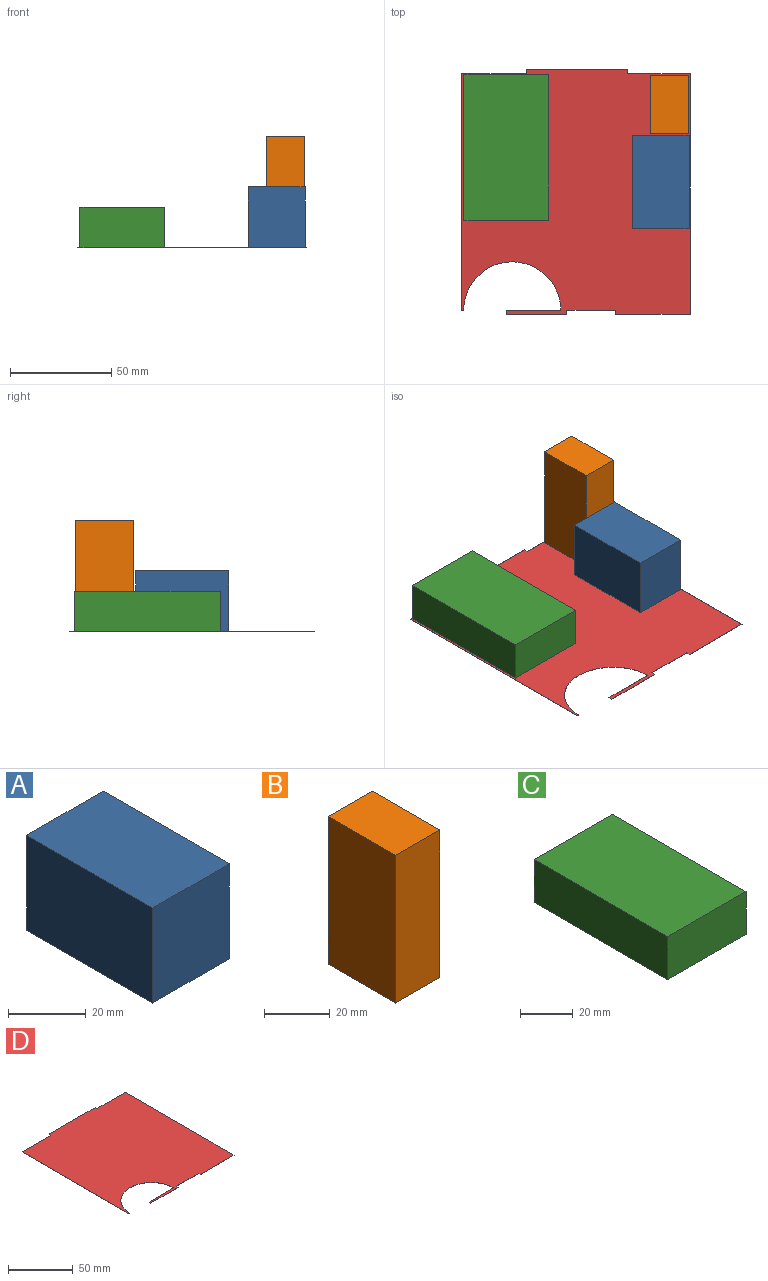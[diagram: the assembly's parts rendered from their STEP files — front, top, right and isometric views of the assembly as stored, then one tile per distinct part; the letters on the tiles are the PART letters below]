
ASSEMBLY  parts=4 mates=3
PART A: 6 faces, bbox 28x46x30 mm
  f0: plane 30x28mm, normal (0,1,0), area 840mm2, adj f1,f3,f4,f5
  f1: plane 46x30mm, normal (-1,0,0), area 1380mm2, adj f0,f2,f4,f5
  f2: plane 30x28mm, normal (0,-1,0), area 840mm2, adj f1,f3,f4,f5
  f3: plane 46x30mm, normal (1,0,0), area 1380mm2, adj f0,f2,f4,f5
  f4: plane 46x28mm, normal (0,0,1), area 1288mm2, adj f0,f1,f2,f3
  f5: plane 46x28mm, normal (0,0,-1), area 1288mm2, adj f0,f1,f2,f3
PART B: 6 faces, bbox 19x29x55 mm
  f0: plane 55x19mm, normal (0,1,0), area 1045mm2, adj f1,f3,f4,f5
  f1: plane 55x29mm, normal (-1,0,0), area 1595mm2, adj f0,f2,f4,f5
  f2: plane 55x19mm, normal (0,-1,0), area 1045mm2, adj f1,f3,f4,f5
  f3: plane 55x29mm, normal (1,0,0), area 1595mm2, adj f0,f2,f4,f5
  f4: plane 29x19mm, normal (0,0,1), area 551mm2, adj f0,f1,f2,f3
  f5: plane 29x19mm, normal (0,0,-1), area 551mm2, adj f0,f1,f2,f3
PART C: 6 faces, bbox 42x72x20 mm
  f0: plane 42x20mm, normal (0,1,0), area 840mm2, adj f1,f3,f4,f5
  f1: plane 72x20mm, normal (-1,0,0), area 1440mm2, adj f0,f2,f4,f5
  f2: plane 42x20mm, normal (0,-1,0), area 840mm2, adj f1,f3,f4,f5
  f3: plane 72x20mm, normal (1,0,0), area 1440mm2, adj f0,f2,f4,f5
  f4: plane 72x42mm, normal (0,0,1), area 3024mm2, adj f0,f1,f2,f3
  f5: plane 72x42mm, normal (0,0,-1), area 3024mm2, adj f0,f1,f2,f3
PART D: 18 faces, bbox 113x121x0.1 mm
  f0: cylinder r=24mm len=48mm, axis (0,0,-1), area 7.5mm2, adj f1,f15,f16,f17
  f1: plane 27x0.1mm, normal (0,1,0), area 2.7mm2, adj f0,f2,f16,f17
  f2: plane 2x0.1mm, normal (-1,0,0), area 0.2mm2, adj f1,f3,f16,f17
  f3: plane 30x0.1mm, normal (0,-1,0), area 3mm2, adj f2,f4,f16,f17
  f4: plane 2x0.1mm, normal (1,0,0), area 0.2mm2, adj f3,f5,f16,f17
  f5: plane 24x0.1mm, normal (0,-1,0), area 2.4mm2, adj f4,f6,f16,f17
  f6: plane 2x0.1mm, normal (-1,0,0), area 0.2mm2, adj f5,f7,f16,f17
  f7: plane 37x0.1mm, normal (0,-1,0), area 3.7mm2, adj f6,f8,f16,f17
  f8: plane 119x0.1mm, normal (1,0,0), area 11.9mm2, adj f7,f9,f16,f17
  f9: plane 31x0.1mm, normal (0,1,0), area 3.1mm2, adj f8,f10,f16,f17
  f10: plane 2x0.1mm, normal (1,0,0), area 0.2mm2, adj f9,f11,f16,f17
  f11: plane 50x0.1mm, normal (0,1,0), area 5mm2, adj f10,f12,f16,f17
  f12: plane 2x0.1mm, normal (-1,0,0), area 0.2mm2, adj f11,f13,f16,f17
  f13: plane 32x0.1mm, normal (0,1,0), area 3.2mm2, adj f12,f14,f16,f17
  f14: plane 117x0.1mm, normal (-1,0,0), area 11.7mm2, adj f13,f15,f16,f17
  f15: plane 1x0.1mm, normal (0,-1,0), area 0.1mm2, adj f0,f14,f16,f17
  f16: plane 121x113mm, normal (0,0,1), area 12550.2mm2, adj f0,f1,f2,f3,f4,f5,f6,f7
  f17: plane 121x113mm, normal (0,0,-1), area 12550.2mm2, adj f0,f1,f2,f3,f4,f5,f6,f7
PLACE A rot(axis=(0,0,-1),180deg) t=(-167.19,12.83,-12.11)mm
PLACE B rot(axis=(0,0,-1),0deg) t=(-174.85,25.58,-12.11)mm
PLACE C rot(axis=(0,0,-1),180deg) t=(27.24,-28.87,-12.11)mm
PLACE D t=(-77.29,-6.38,-12.11)mm
MATE planar C.f5 <-> D.f16  axis (0,0,-1) through (-112.35,14.14,-12.01)mm
MATE planar A.f5 <-> D.f16  axis (0,0,-1) through (-36.13,-3.03,-12.01)mm
MATE planar B.f5 <-> D.f16  axis (0,0,-1) through (-31.67,35.31,-12.01)mm
